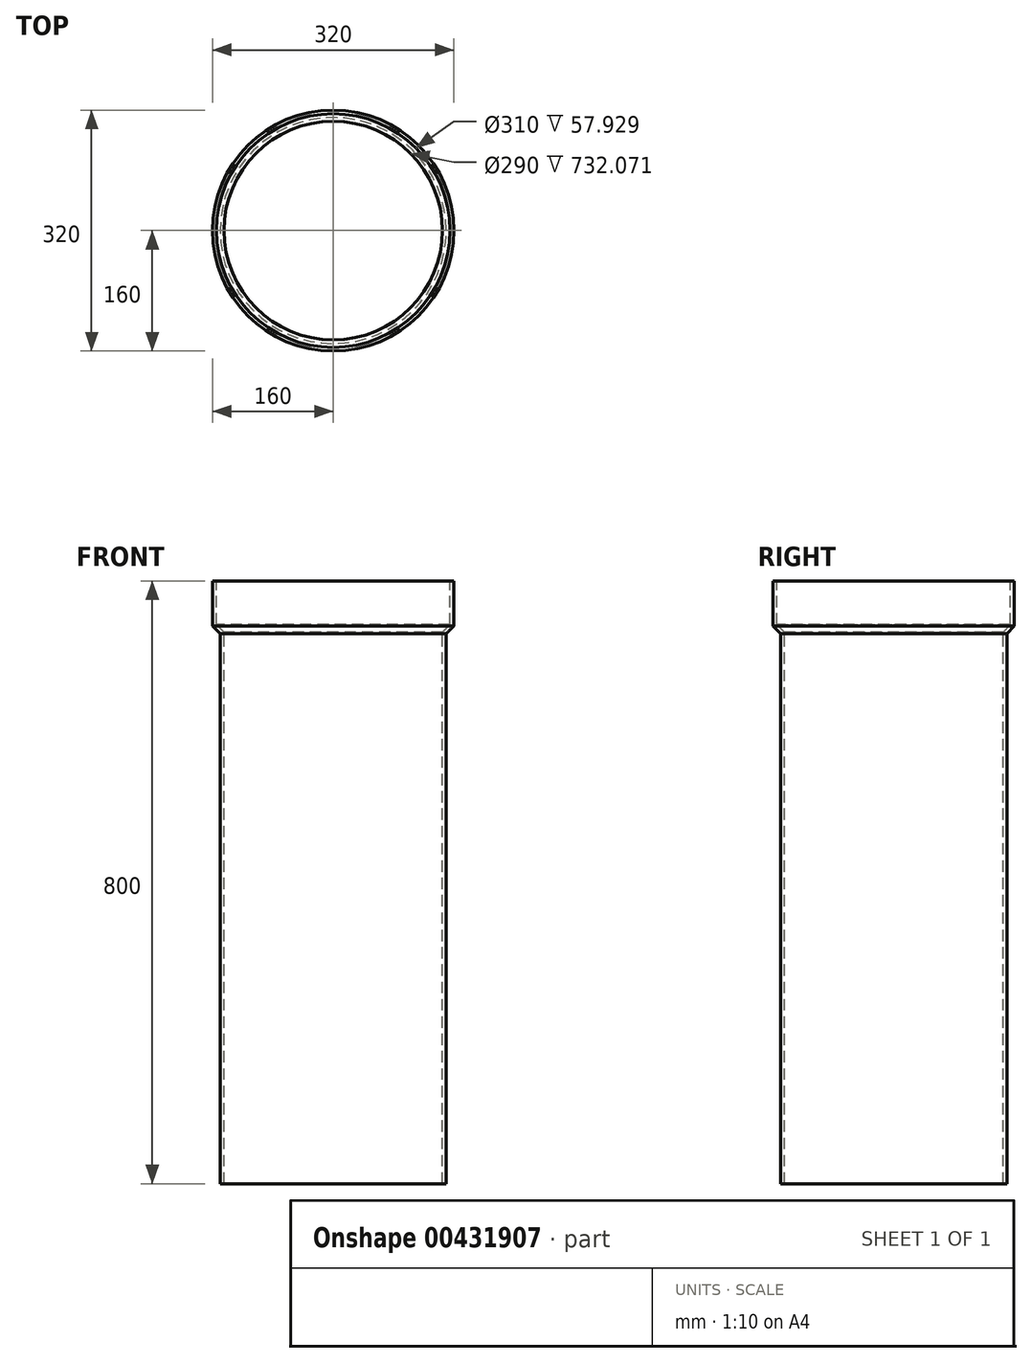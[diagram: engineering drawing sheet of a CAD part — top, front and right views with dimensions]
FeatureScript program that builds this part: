
annotation { "Feature Type Name" : "Feature", "Feature Type Description" : "" }
export const myFeature = defineFeature(function(context is Context, id is Id, definition is map)
    precondition{}
    {
        {
            var Q0;
            Q0=qCreatedBy(makeId("Front.planeOp"),FACE);
            var sketch = newSketch(context, id + "F0", { "sketchPlane" : qUnion([Q0])});
            skLineSegment(sketch, "E0", {"start": v(-160, 0) * mm, "end": v(-160, -60) * mm});
            skLineSegment(sketch, "E1", {"start": v(-160, -60) * mm, "end": v(-150, -70) * mm});
            skLineSegment(sketch, "E2", {"start": v(-150, -70) * mm, "end": v(-150, -800) * mm});
            skLineSegment(sketch, "E3", {"start": v(0, 0) * mm, "end": v(0, -800) * mm});
            skLineSegment(sketch, "E4", {"start": v(0, 0) * mm, "end": v(-160, 0) * mm});
            skLineSegment(sketch, "E5", {"start": v(-150, -800) * mm, "end": v(0, -800) * mm});
            skPoint(sketch, "E6.orphan", {"position": v(0, 93.86) * mm});
            skPoint(sketch, "E7.orphan", {"position": v(0, -828.42) * mm});
            skSolve(sketch);
        }
        {
            var Q0;
            Q0=makeQuery(id+"F0.imprint","IMPRINT",FACE,{"disambiguationData":[TD([[makeQuery(id+"F0.imprint","IMPRINT",EDGE,{"derivedFrom":sQuery(id+"F0.wireOp",EDGE,"E0")}),1.0]])]});
            var Q1;
            Q1=sQuery(id+"F0.wireOp",EDGE,"E3");
            revolve(context, id + "F1", {"entities" : qUnion([Q0]), "axis" : qUnion([Q1]), "revolveType" : RevolveType.FULL});
        }
        {
            var Q0;
            Q0=makeQuery(id+"F1.opRevolve","SWEPT_FACE",FACE,{"disambiguationData":[OSD([sQuery(id+"F0.wireOp",EDGE,"E4")])]});
            var Q1;
            Q1=makeQuery(id+"F1.opRevolve","SWEPT_FACE",FACE,{"disambiguationData":[OSD([sQuery(id+"F0.wireOp",EDGE,"E5")])]});
            shell(context, id + "F2", {"entities" : qUnion([Q0, Q1]), "thickness" : 5 * mm});
        }
    });
